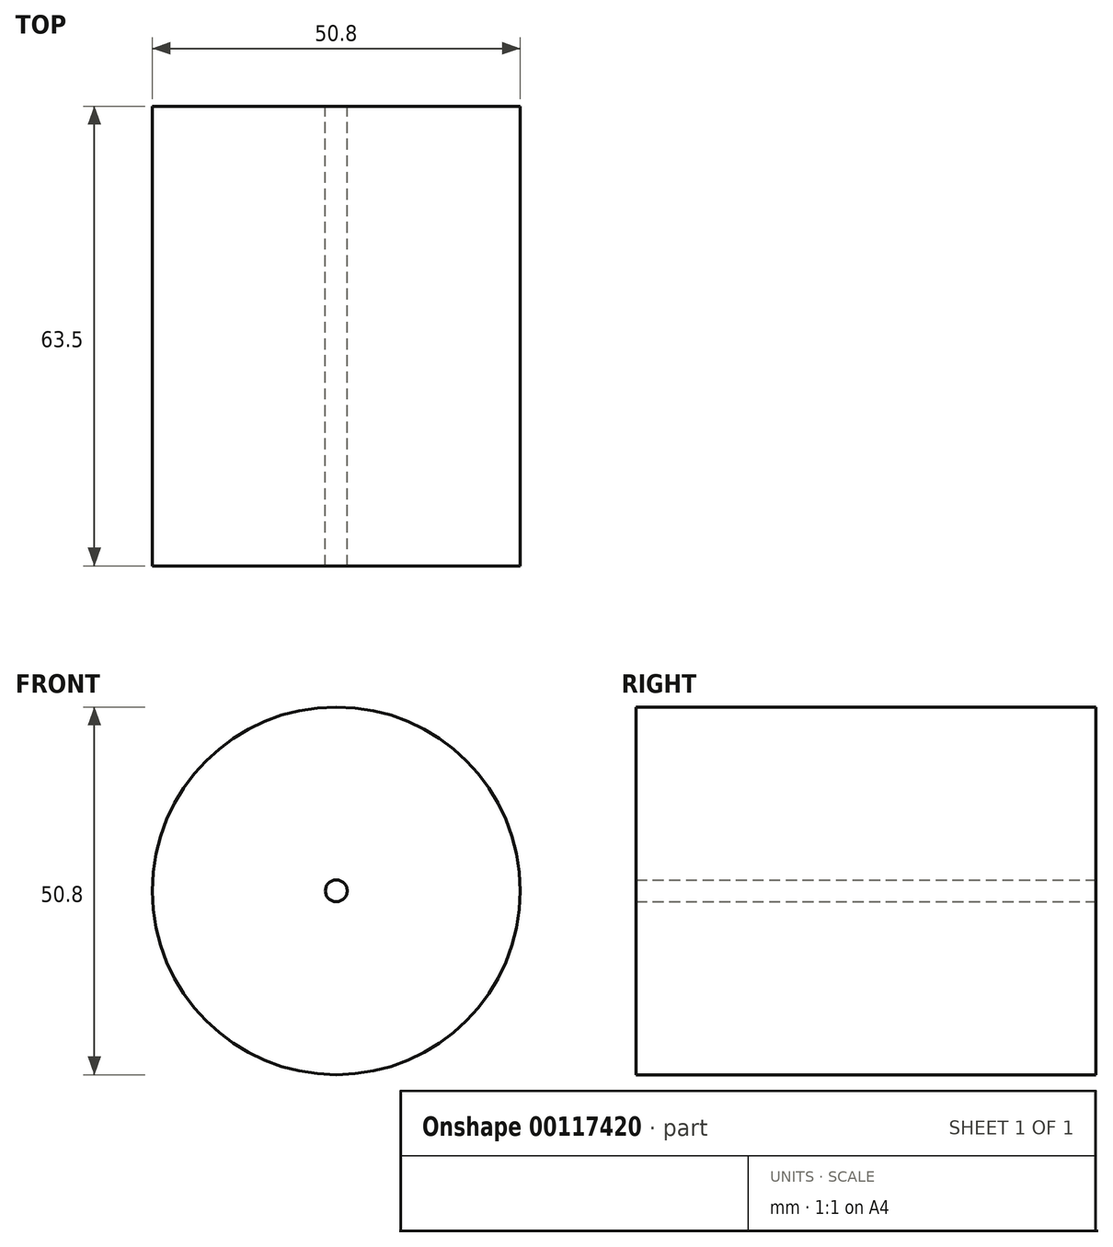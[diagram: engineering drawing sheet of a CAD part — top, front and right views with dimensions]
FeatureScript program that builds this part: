
annotation { "Feature Type Name" : "Feature", "Feature Type Description" : "" }
export const myFeature = defineFeature(function(context is Context, id is Id, definition is map)
    precondition{}
    {
        {
            var Q0;
            Q0=qCreatedBy(makeId("Front.planeOp"),FACE);
            var sketch = newSketch(context, id + "F0", { "sketchPlane" : qUnion([Q0])});
            skCircle(sketch, "E0", {"center": v(-39.03, 20.94) * mm, "radius": 25.4 * mm});
            skCircle(sketch, "E1", {"center": v(-39.03, 20.94) * mm, "radius": 1.5 * mm});
            skSolve(sketch);
        }
        {
            var Q0;
            Q0=makeQuery(id+"F0.imprint","IMPRINT",FACE,{"disambiguationData":[TD([[makeQuery(id+"F0.imprint","IMPRINT",EDGE,{"derivedFrom":sQuery(id+"F0.wireOp",EDGE,"E0")}),1.0]])]});
            var Q1;
            Q1=sQuery(id+"F0.wireOp",EDGE,"E0");
            var Q2;
            Q2=sQuery(id+"F0.wireOp",EDGE,"E1");
            extrude(context, id + "F1", {"entities" : qUnion([Q0]), "surfaceEntities" : qUnion([Q1, Q2]), "depth" : 63.5 * mm});
        }
    });
